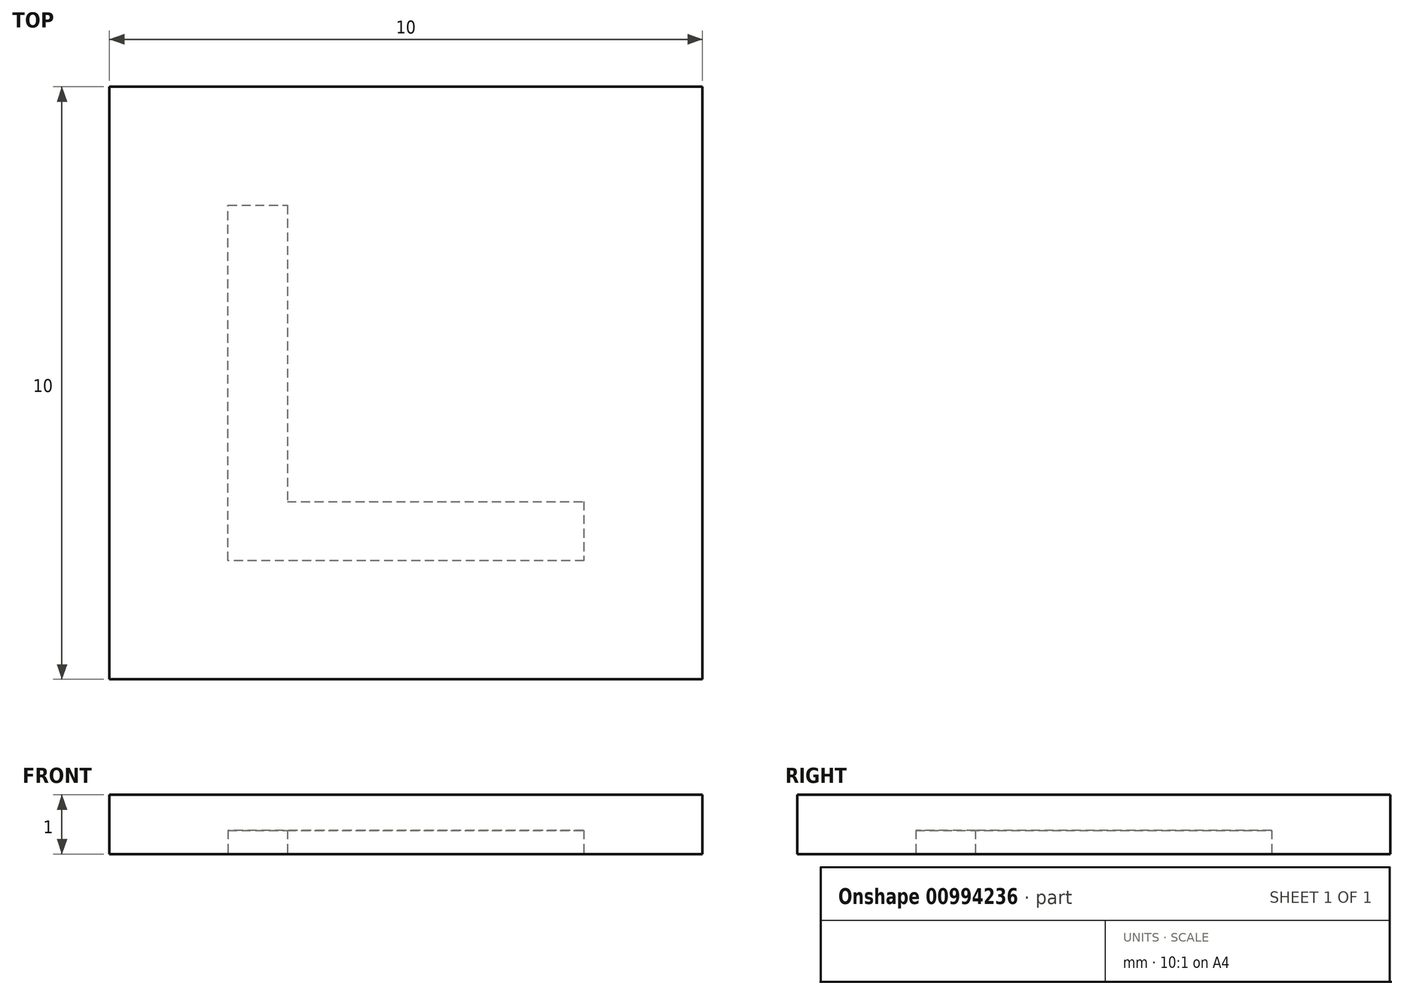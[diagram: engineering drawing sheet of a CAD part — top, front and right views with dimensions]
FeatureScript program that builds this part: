
annotation { "Feature Type Name" : "Feature", "Feature Type Description" : "" }
export const myFeature = defineFeature(function(context is Context, id is Id, definition is map)
    precondition{}
    {
        {
            var Q0;
            Q0=qCreatedBy(makeId("Top.planeOp"),FACE);
            var sketch = newSketch(context, id + "F0", { "sketchPlane" : qUnion([Q0])});
            skLineSegment(sketch, "E0.bottom", {"start": v(-5, 5) * mm, "end": v(5, 5) * mm});
            skLineSegment(sketch, "E0.top", {"start": v(-5, -5) * mm, "end": v(5, -5) * mm});
            skLineSegment(sketch, "E0.left", {"start": v(-5, 5) * mm, "end": v(-5, -5) * mm});
            skLineSegment(sketch, "E0.right", {"start": v(5, 5) * mm, "end": v(5, -5) * mm});
            skPoint(sketch, "E1", {"position": v(0, 5) * mm});
            skPoint(sketch, "E2", {"position": v(-5, 0) * mm});
            skSolve(sketch);
        }
        {
            var Q0;
            Q0 = qSketchRegion(id + "F0", true);
            extrude(context, id + "F1", {"entities" : qUnion([Q0]), "depth" : 1 * mm, "offsetDistance" : 25 * mm});
        }
        {
            var Q0;
            Q0=makeQuery(id+"F1.opExtrude","CAP_FACE",FACE,{"disambiguationData":[OSD([sQuery(id+"F0.wireOp",EDGE,"E0.bottom"),sQuery(id+"F0.wireOp",EDGE,"E0.top"),sQuery(id+"F0.wireOp",EDGE,"E0.left"),sQuery(id+"F0.wireOp",EDGE,"E0.right")])],"isStart":true});
            var sketch = newSketch(context, id + "F2", { "sketchPlane" : qUnion([Q0])});
            skLineSegment(sketch, "E3", {"start": v(3, 3) * mm, "end": v(-3, 3) * mm});
            skLineSegment(sketch, "E4", {"start": v(-3, 3) * mm, "end": v(-3, -3) * mm});
            skLineSegment(sketch, "E5", {"start": v(-3, -3) * mm, "end": v(-2, -3) * mm});
            skLineSegment(sketch, "E6", {"start": v(-2, -3) * mm, "end": v(-2, 2) * mm});
            skLineSegment(sketch, "E7", {"start": v(-2, 2) * mm, "end": v(3, 2) * mm});
            skLineSegment(sketch, "E8", {"start": v(3, 2) * mm, "end": v(3, 3) * mm});
            skSolve(sketch);
        }
        {
            var Q0;
            Q0 = qSketchRegion(id + "F2", true);
            extrude(context, id + "F3", {"entities" : qUnion([Q0]), "operationType" : NewBodyOperationType.REMOVE, "oppositeDirection" : true, "depth" : 0.4 * mm, "offsetDistance" : 25 * mm});
        }
    });
